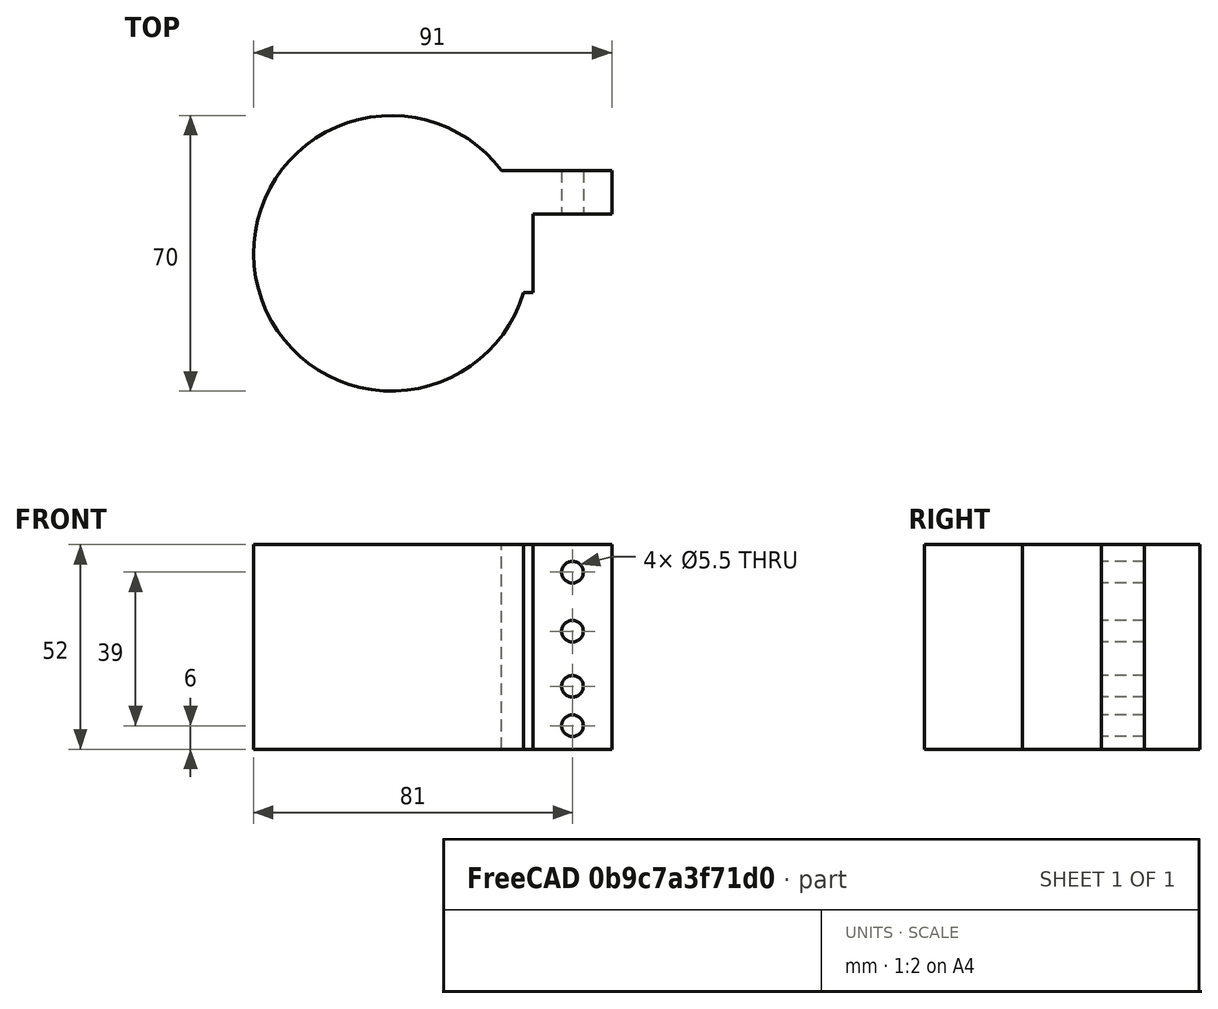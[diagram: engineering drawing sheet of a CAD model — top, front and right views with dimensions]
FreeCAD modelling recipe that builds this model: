
FCSTD DOCUMENT  (FreeCAD 0.17R13522 (Git))
Label: utm-mock
License: All rights reserved
LicenseURL: http://en.wikipedia.org/wiki/All_rights_reserved
objects: Part::Cylinder×5, Part::Box×2, Part::MultiFuse×2, Part::Cut×1
note: 10 computed .brp shape members not serialized (recipe doc carries the construction recipe); baked Part::Feature solids carry a one-line shape summary decoded from their .brp

FEATURE [Part::Cylinder] Cylinder
  Angle = 360
  AttacherType = Attacher::AttachEngine3D
  Height = 15
  Placement = pos=(46,23,30) rot=(1,0,0;1.5708rad)
  Radius = 2.75
FEATURE [Part::Cylinder] Cylinder001
  Angle = 360
  AttacherType = Attacher::AttachEngine3D
  Height = 15
  Placement = pos=(46,23,6) rot=(1,0,0;1.5708rad)
  Radius = 2.75
FEATURE [Part::Cylinder] Cylinder002
  Angle = 360
  AttacherType = Attacher::AttachEngine3D
  Height = 15
  Placement = pos=(46,23,16) rot=(1,0,0;1.5708rad)
  Radius = 2.75
FEATURE [Part::Cylinder] Cylinder003
  Angle = 360
  AttacherType = Attacher::AttachEngine3D
  Height = 15
  Placement = pos=(46,23,45) rot=(1,0,0;1.5708rad)
  Radius = 2.75
FEATURE [Part::Cylinder] Cylinder004
  Angle = 360
  AttacherType = Attacher::AttachEngine3D
  Height = 52
  Radius = 35
FEATURE [Part::Box] Box  label="Cube"
  AttacherType = Attacher::AttachEngine3D
  Height = 52
  Length = 20
  Placement = pos=(36,10,0) rot=(0,0,1;0rad)
  Width = 11
FEATURE [Part::Box] Box001  label="Cube001"
  AttacherType = Attacher::AttachEngine3D
  Height = 52
  Length = 10
  Placement = pos=(26,-10,0) rot=(0,0,1;0rad)
  Width = 31
FEATURE [Part::MultiFuse] Fusion  label="Negative Fusion"
  Shapes = -> [Cylinder,Cylinder001,Cylinder002,Cylinder003]
FEATURE [Part::MultiFuse] Fusion001  label="Positive Fusion"
  Shapes = -> [Cylinder004,Box,Box001]
FEATURE [Part::Cut] Cut
  Base = -> Fusion001
  Tool = -> Fusion
